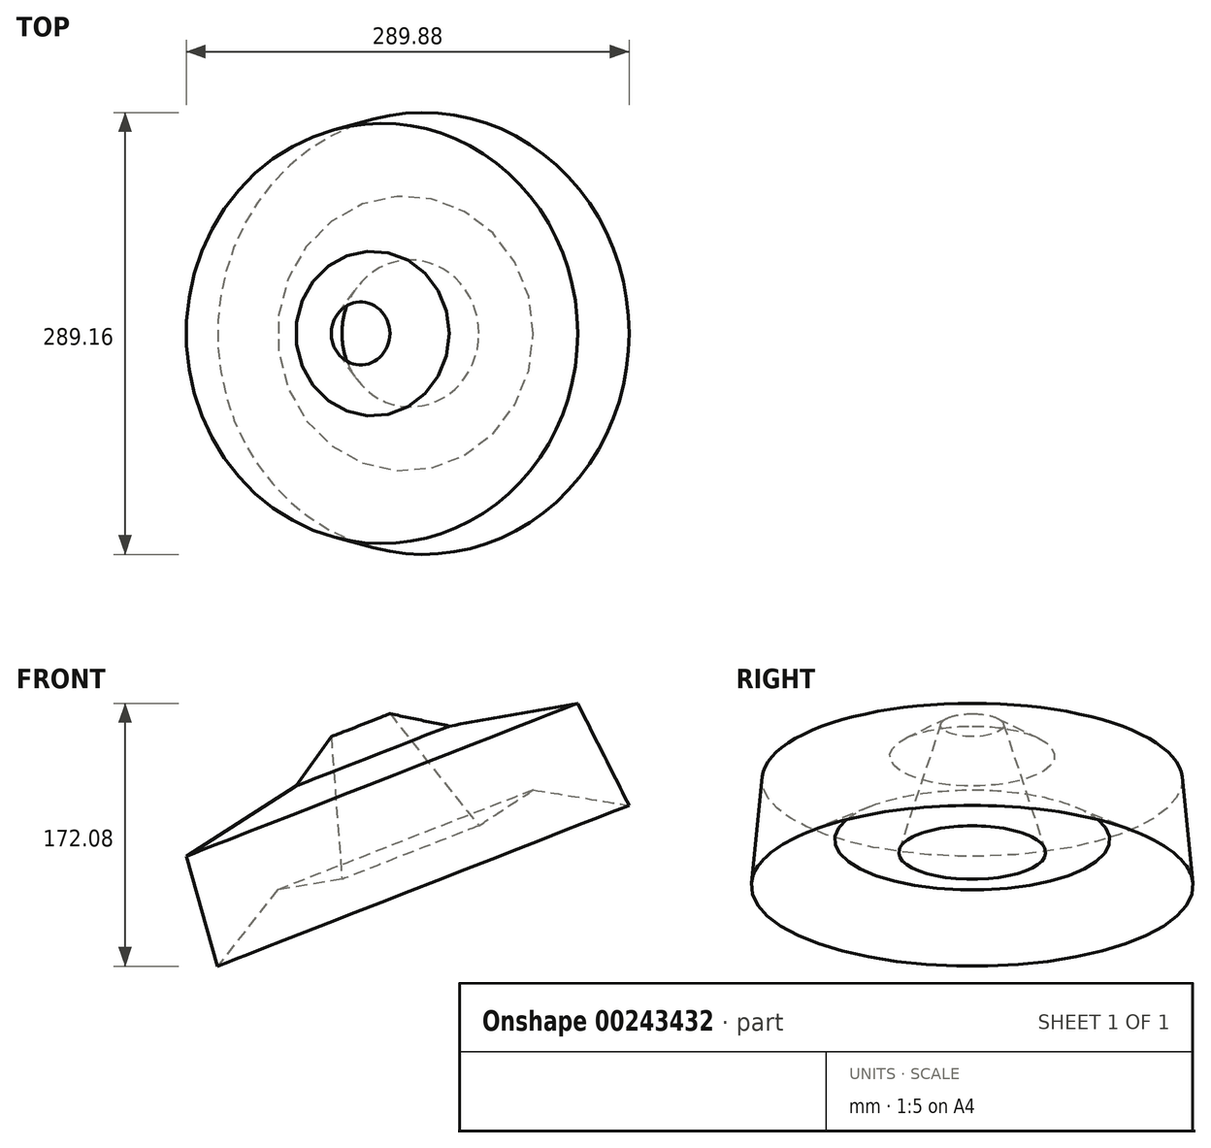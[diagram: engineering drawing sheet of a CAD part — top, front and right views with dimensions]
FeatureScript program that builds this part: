
annotation { "Feature Type Name" : "Feature", "Feature Type Description" : "" }
export const myFeature = defineFeature(function(context is Context, id is Id, definition is map)
    precondition{}
    {
        {
            var Q0;
            Q0=qCreatedBy(makeId("Front.planeOp"),FACE);
            var sketch = newSketch(context, id + "F0", { "sketchPlane" : qUnion([Q0])});
            skLineSegment(sketch, "E0", {"start": v(-99.07, 38.63) * mm, "end": v(-40.91, -34.73) * mm});
            skLineSegment(sketch, "E1", {"start": v(-40.91, -34.73) * mm, "end": v(-5.15, -11.22) * mm});
            skLineSegment(sketch, "E2", {"start": v(-5.15, -11.22) * mm, "end": v(57.47, -21.36) * mm});
            skLineSegment(sketch, "E3", {"start": v(57.47, -21.36) * mm, "end": v(23.8, 45.45) * mm});
            skLineSegment(sketch, "E4", {"start": v(23.8, 45.45) * mm, "end": v(-60.14, 30.54) * mm});
            skLineSegment(sketch, "E5", {"start": v(-60.14, 30.54) * mm, "end": v(-99.07, 38.63) * mm});
            skLineSegment(sketch, "E6", {"start": v(-124.74, 47.66) * mm, "end": v(-82.22, -61.12) * mm});
            skSolve(sketch);
        }
        {
            var Q0;
            Q0=makeQuery(id+"F0.imprint","IMPRINT",FACE,{"disambiguationData":[TD([[makeQuery(id+"F0.imprint","IMPRINT",EDGE,{"derivedFrom":sQuery(id+"F0.wireOp",EDGE,"E0")}),1.0]])]});
            var Q1;
            Q1=sQuery(id+"F0.wireOp",EDGE,"E6");
            revolve(context, id + "F1", {"entities" : qUnion([Q0]), "axis" : qUnion([Q1]), "revolveType" : RevolveType.FULL});
        }
    });
